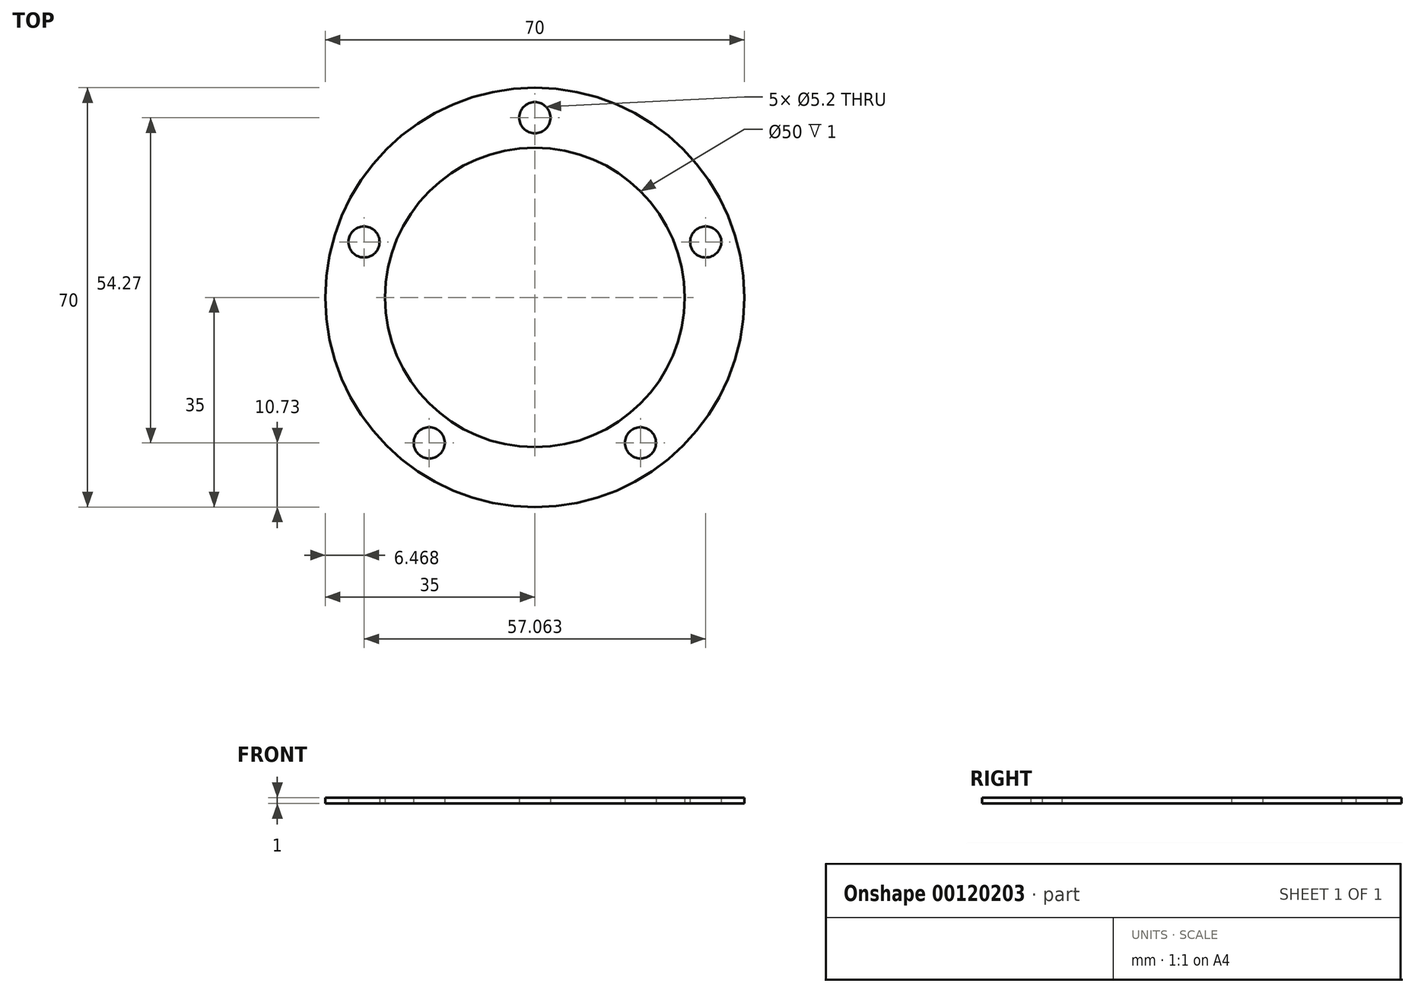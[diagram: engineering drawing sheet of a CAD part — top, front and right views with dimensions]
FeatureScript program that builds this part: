
annotation { "Feature Type Name" : "Feature", "Feature Type Description" : "" }
export const myFeature = defineFeature(function(context is Context, id is Id, definition is map)
    precondition{}
    {
        {
            var Q0;
            Q0=qCreatedBy(makeId("Top.planeOp"),FACE);
            var sketch = newSketch(context, id + "F0", { "sketchPlane" : qUnion([Q0])});
            skCircle(sketch, "E0", {"center": v(0, 0) * mm, "radius": 25 * mm});
            skCircle(sketch, "E1", {"center": v(0, 0) * mm, "radius": 35 * mm});
            skPoint(sketch, "E2", {"position": v(0, 30) * mm});
            skCircle(sketch, "E3", {"center": v(0, 30) * mm, "radius": 2.6 * mm});
            skCircle(sketch, "E4.1.0", {"center": v(-28.53, 9.27) * mm, "radius": 2.6 * mm});
            skCircle(sketch, "E4.2.0", {"center": v(-17.63, -24.27) * mm, "radius": 2.6 * mm});
            skCircle(sketch, "E5.1.3.0", {"center": v(17.63, -24.27) * mm, "radius": 2.6 * mm});
            skCircle(sketch, "E5.1.4.0", {"center": v(28.53, 9.27) * mm, "radius": 2.6 * mm});
            skSolve(sketch);
        }
        {
            var Q0;
            Q0=makeQuery(id+"F0.imprint","IMPRINT",FACE,{"disambiguationData":[TD([[makeQuery(id+"F0.imprint","IMPRINT",EDGE,{"derivedFrom":sQuery(id+"F0.wireOp",EDGE,"E0")}),-1.0]])]});
            extrude(context, id + "F1", {"entities" : qUnion([Q0]), "depth" : 1 * mm});
        }
    });
